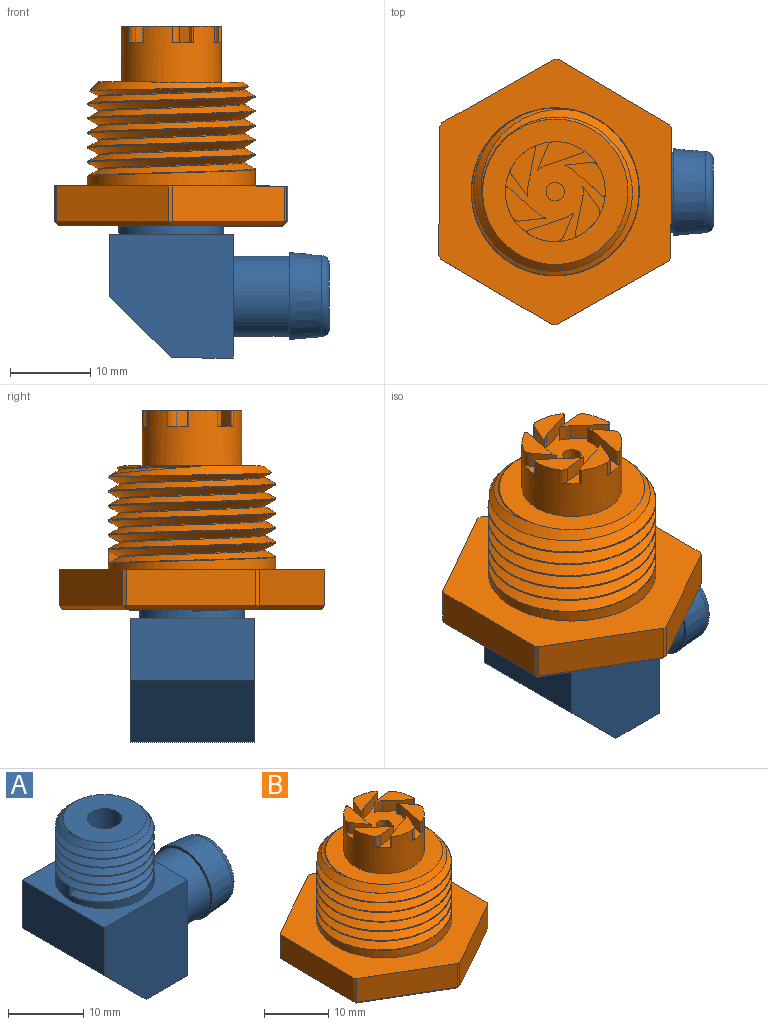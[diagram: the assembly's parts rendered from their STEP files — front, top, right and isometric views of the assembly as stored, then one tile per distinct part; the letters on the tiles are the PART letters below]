
ASSEMBLY  parts=2 mates=1
PART A: 29 faces, bbox 27.5x15.5x26.2 mm
  f0: plane 15.5x15.5mm, normal (0,1,0), area 210.2mm2, adj f1,f10,f11,f12,f28
  f1: plane 15.5x7.75mm, normal (-1,0,0), area 120.1mm2, adj f0,f2,f11,f28
  f2: plane 15.5x15.5mm, normal (0,-1,0), area 210.2mm2, adj f1,f10,f11,f12,f28
  f3: cylinder r=6.56mm len=13.13mm, axis (0,0,-1), area 63.7mm2, adj f4,f11,f22,f27
  f4: cylinder r=6.56mm len=13.13mm, axis (0,0,-1), area 0.1mm2, adj f3,f5,f23,f27
  f5: cylinder r=6.56mm len=13.13mm, axis (0,0,-1), area 0.1mm2, adj f4,f6,f23,f27
  f6: cylinder r=6.56mm len=13.13mm, axis (0,0,-1), area 0.1mm2, adj f5,f7,f23,f27
  f7: cylinder r=6.56mm len=13.13mm, axis (0,0,-1), area 0.1mm2, adj f6,f8,f23,f27
  f8: cylinder r=6.56mm len=13.13mm, axis (0,0,-1), area 0mm2, adj f7,f21,f23,f27
  f9: cylinder r=5mm len=10mm, axis (-1,0,0), area 219.9mm2, adj f10,f16
  f10: plane 15.5x15.5mm, normal (1,0,0), area 161.7mm2, adj f0,f2,f9,f11,f12
  f11: plane 15.5x15.5mm, normal (0,0,1), area 104.8mm2, adj f0,f1,f2,f3,f10
  f12: plane 15.5x7.75mm, normal (0,0,-1), area 120.1mm2, adj f0,f2,f10,f28
  f13: cylinder r=2.3mm len=10.75mm, axis (0,0,-1), area 155.4mm2, adj f14,f19
  f14: plane 11.04x11.03mm, normal (0,0,1), area 78.9mm2, adj f13,f21,f25
  f15: cone r=5mm half-angle=5deg, axis (-1,0,0), area 135.6mm2, adj f16,f20
  f16: plane 10.88x10.88mm, normal (-1,0,0), area 14.3mm2, adj f9,f15
  f17: cylinder r=2.3mm len=12.75mm, axis (-1,0,0), area 184.3mm2, adj f18,f19
  f18: plane 8.17x8.17mm, normal (1,0,0), area 35.8mm2, adj f17,f20
  f19: torus R=7mm, axis (0,-1,0), area 158.9mm2, adj f13,f17
  f20: torus R=4.08mm, axis (1,0,0), area 43.8mm2, adj f15,f18
  f21: cone r=5.51mm half-angle=45deg, axis (0,0,-1), area 27.1mm2, adj f8,f14,f23,f24,f25,f26,f27
  f22: plane 1.41x1.07mm, normal (0,-1,0), area 0.7mm2, adj f3,f23,f24,f25,f26,f27
  f23: bspline ~15.16x13.13mm, area 16.5mm2, adj f4,f5,f6,f7,f8,f21,f22,f24
  f24: bspline ~15.07x13.05mm, area 230.4mm2, adj f21,f22,f23,f25
  f25: bspline ~12.81x11.09mm, area 34.8mm2, adj f14,f21,f22,f24,f26
  f26: bspline ~15.07x13.05mm, area 252.3mm2, adj f21,f22,f25,f27
  f27: bspline ~15.16x13.13mm, area 19.8mm2, adj f3,f4,f5,f6,f7,f8,f21,f22
  f28: plane 15.5x7.75mm, normal (-0.71,0,-0.71), area 169.9mm2, adj f0,f1,f2,f12
PART B: 91 faces, bbox 29.2x33.2x25.6 mm
  f0: cylinder r=5.85mm len=11.69mm, axis (0,0,1), area 25.2mm2, adj f55,f65,f67
  f1: cylinder r=10.5mm len=21mm, axis (0,0,-1), area 107.4mm2, adj f2,f52,f58,f63
  f2: cylinder r=10.5mm len=21mm, axis (0,0,-1), area 0.5mm2, adj f1,f3,f59,f63
  f3: cylinder r=10.5mm len=21mm, axis (0,0,-1), area 0.5mm2, adj f2,f4,f59,f63
  f4: cylinder r=10.5mm len=21mm, axis (0,0,-1), area 0.5mm2, adj f3,f5,f59,f63
  f5: cylinder r=10.5mm len=21mm, axis (0,0,-1), area 0.5mm2, adj f4,f6,f59,f63
  f6: cylinder r=10.5mm len=21mm, axis (0,0,-1), area 0.5mm2, adj f5,f57,f59,f63
  f7: plane 5.08x4.27mm, normal (0,0,1), area 9.6mm2, adj f30,f31,f32,f35,f36,f44
  f8: plane 5.83x3.59mm, normal (0,0,1), area 9.6mm2, adj f26,f27,f28,f29,f32,f43
  f9: plane 6.26x3.1mm, normal (0,0,1), area 9.6mm2, adj f22,f23,f24,f25,f32,f42
  f10: plane 5.08x4.27mm, normal (0,0,1), area 9.6mm2, adj f18,f19,f20,f21,f32,f41
  f11: plane 5.83x3.59mm, normal (0,0,1), area 9.6mm2, adj f14,f15,f16,f17,f32,f40
  f12: cylinder r=0.2mm len=2mm, axis (0,0,1), area 0.9mm2, adj f13,f32,f33,f39
  f13: plane 4.7x2mm, normal (0.98,-0.2,0), area 9.6mm2, adj f12,f33,f39,f45
  f14: plane 3x2mm, normal (-0.92,0.4,0), area 6.5mm2, adj f11,f15,f39,f40
  f15: cylinder r=0.97mm len=2mm, axis (0,0,1), area 2.2mm2, adj f11,f14,f32,f39
  f16: cylinder r=0.2mm len=2mm, axis (0,0,1), area 0.9mm2, adj f11,f17,f32,f39
  f17: plane 4.55x2mm, normal (0.32,-0.95,0), area 9.6mm2, adj f11,f16,f39,f40
  f18: plane 3.25x2mm, normal (-0.11,0.99,0), area 6.5mm2, adj f10,f19,f39,f41
  f19: cylinder r=0.97mm len=2mm, axis (0,0,1), area 2.2mm2, adj f10,f18,f32,f39
  f20: cylinder r=0.2mm len=2mm, axis (0,0,1), area 0.9mm2, adj f10,f21,f32,f39
  f21: plane 3.6x3.17mm, normal (-0.66,-0.75,0), area 9.6mm2, adj f10,f20,f39,f41
  f22: plane 2.63x2mm, normal (0.8,0.6,0), area 6.5mm2, adj f9,f23,f39,f42
  f23: cylinder r=0.97mm len=2mm, axis (0,0,1), area 2.2mm2, adj f9,f22,f32,f39
  f24: cylinder r=0.2mm len=2mm, axis (0,0,1), area 0.9mm2, adj f9,f25,f32,f39
  f25: plane 4.7x2mm, normal (-0.98,0.2,0), area 9.6mm2, adj f9,f24,f39,f42
  f26: plane 3x2mm, normal (0.92,-0.4,0), area 6.5mm2, adj f8,f27,f39,f43
  f27: cylinder r=0.97mm len=2mm, axis (0,0,1), area 2.2mm2, adj f8,f26,f32,f39
  f28: cylinder r=0.2mm len=2mm, axis (0,0,1), area 0.9mm2, adj f8,f29,f32,f39
  f29: plane 4.55x2mm, normal (-0.32,0.95,0), area 9.6mm2, adj f8,f28,f39,f43
  f30: plane 3.25x2mm, normal (0.11,-0.99,0), area 6.5mm2, adj f7,f31,f39,f44
  f31: cylinder r=0.97mm len=2mm, axis (0,0,1), area 2.2mm2, adj f7,f30,f32,f39
  f32: cylinder r=6.25mm len=12.5mm, axis (0,0,1), area 241.6mm2, adj f7,f8,f9,f10,f11,f12,f15,f16
  f33: plane 6.26x3.1mm, normal (0,0,1), area 9.6mm2, adj f12,f13,f32,f37,f38,f45
  f34: plane 18.18x18.18mm, normal (0,0,1), area 136.7mm2, adj f32,f57
  f35: cylinder r=0.2mm len=2mm, axis (0,0,1), area 0.9mm2, adj f7,f32,f36,f39
  f36: plane 3.6x3.17mm, normal (0.66,0.75,0), area 9.6mm2, adj f7,f35,f39,f44
  f37: plane 2.63x2mm, normal (-0.8,-0.6,0), area 6.5mm2, adj f33,f38,f39,f45
  f38: cylinder r=0.97mm len=2mm, axis (0,0,1), area 2.2mm2, adj f32,f33,f37,f39
  f39: plane 12.5x12.47mm, normal (0,0,1), area 61mm2, adj f12,f13,f14,f15,f16,f17,f18,f19
  f40: extruded ~2x1.15mm, area 2.7mm2, adj f11,f14,f17,f39
  f41: extruded ~2x1.14mm, area 2.7mm2, adj f10,f18,f21,f39
  f42: extruded ~2x1.32mm, area 2.7mm2, adj f9,f22,f25,f39
  f43: extruded ~2x1.15mm, area 2.7mm2, adj f8,f26,f29,f39
  f44: extruded ~2x1.14mm, area 2.7mm2, adj f7,f30,f36,f39
  f45: extruded ~2x1.32mm, area 2.7mm2, adj f13,f33,f37,f39
  f46: plane 13.93x8.21mm, normal (0.51,0.86,0), area 72.7mm2, adj f52,f80,f86,f89
  f47: plane 14.07x7.96mm, normal (-0.49,0.87,0), area 72.7mm2, adj f52,f74,f80,f81
  f48: plane 16.17x4.5mm, normal (-1,0.01,0), area 72.7mm2, adj f52,f72,f74,f75
  f49: plane 13.93x8.21mm, normal (-0.51,-0.86,0), area 72.7mm2, adj f52,f72,f76,f77
  f50: plane 14.07x7.96mm, normal (0.49,-0.87,0), area 72.7mm2, adj f52,f77,f82,f83
  f51: plane 16.17x4.5mm, normal (1,-0.01,0), area 72.7mm2, adj f52,f83,f87,f89
  f52: plane 33.2x29.14mm, normal (0,0,1), area 381.9mm2, adj f1,f46,f47,f48,f49,f50,f51,f72
  f53: plane 32.35x28.16mm, normal (0,0,-1), area 529.6mm2, adj f64,f69,f75,f76,f81,f82,f86,f87
  f54: cone r=2.13mm half-angle=4deg, axis (0,0,-1), area 140.6mm2, adj f39,f90
  f55: plane 11.69x11.69mm, normal (0,0,-1), area 107.3mm2, adj f0,f66
  f56: cylinder r=5.85mm len=11.69mm, axis (0,0,1), area 0mm2, adj f64,f67,f71
  f57: cone r=9.09mm half-angle=45deg, axis (0,0,-1), area 60.1mm2, adj f6,f34,f59,f60,f61,f62,f63
  f58: plane 1.82x1.42mm, normal (-1,0,0), area 1.3mm2, adj f1,f59,f60,f61,f62,f63
  f59: bspline ~24.24x21mm, area 27.6mm2, adj f2,f3,f4,f5,f6,f57,f58,f60
  f60: bspline ~24.15x20.92mm, area 528.9mm2, adj f57,f58,f59,f61
  f61: bspline ~21.08x18.26mm, area 59.9mm2, adj f57,f58,f60,f62
  f62: bspline ~24.15x20.92mm, area 577.7mm2, adj f57,f58,f61,f63
  f63: bspline ~24.24x21mm, area 32.9mm2, adj f1,f2,f3,f4,f5,f6,f57,f58
  f64: cone r=6.9mm half-angle=45deg, axis (0,0,-1), area 30.1mm2, adj f53,f56,f67,f68,f69,f70,f71
  f65: plane 1.42x1.07mm, normal (0,-1,0), area 0.7mm2, adj f0,f66,f67,f68,f69,f70,f71
  f66: cylinder r=5.85mm len=0.51mm, axis (0,0,1), area 0mm2, adj f55,f65,f67
  f67: bspline ~13.56x12.2mm, area 17.4mm2, adj f0,f56,f64,f65,f66,f68
  f68: bspline ~15.82x14.23mm, area 262.1mm2, adj f64,f65,f67,f69
  f69: bspline ~15.96x14.35mm, area 42.8mm2, adj f53,f64,f65,f68,f70
  f70: bspline ~15.82x14.23mm, area 240mm2, adj f64,f65,f69,f71
  f71: bspline ~13.56x12.2mm, area 14.5mm2, adj f56,f64,f65,f70
  f72: plane 4.5x0.44mm, normal (-0.87,-0.49,0), area 2.2mm2, adj f48,f49,f52,f73
  f73: plane 0.5x0.5mm, normal (-0.66,-0.37,-0.65), area 0.2mm2, adj f72,f75,f76
  f74: plane 4.5x0.43mm, normal (-0.86,0.51,0), area 2.2mm2, adj f47,f48,f52,f78
  f75: plane 16.17x0.65mm, normal (-0.71,0.01,-0.71), area 11.4mm2, adj f48,f53,f73,f78
  f76: plane 14.18x8.64mm, normal (-0.36,-0.61,-0.71), area 11.4mm2, adj f49,f53,f73,f79
  f77: plane 4.5x0.5mm, normal (-0.01,-1,0), area 2.2mm2, adj f49,f50,f52,f79
  f78: plane 0.5x0.5mm, normal (-0.65,0.38,-0.65), area 0.2mm2, adj f74,f75,f81
  f79: plane 0.5x0.5mm, normal (-0.01,-0.76,-0.65), area 0.2mm2, adj f76,f77,f82
  f80: plane 4.5x0.5mm, normal (0.01,1,0), area 2.2mm2, adj f46,f47,f52,f84
  f81: plane 14.32x8.39mm, normal (-0.35,0.62,-0.71), area 11.4mm2, adj f47,f53,f78,f84
  f82: plane 14.32x8.39mm, normal (0.35,-0.62,-0.71), area 11.4mm2, adj f50,f53,f79,f85
  f83: plane 4.5x0.43mm, normal (0.86,-0.51,0), area 2.2mm2, adj f50,f51,f52,f85
  f84: plane 0.5x0.5mm, normal (0.01,0.76,-0.65), area 0.2mm2, adj f80,f81,f86
  f85: plane 0.5x0.5mm, normal (0.65,-0.38,-0.65), area 0.2mm2, adj f82,f83,f87
  f86: plane 14.18x8.64mm, normal (0.36,0.61,-0.71), area 11.4mm2, adj f46,f53,f84,f88
  f87: plane 16.17x0.65mm, normal (0.71,-0.01,-0.71), area 11.4mm2, adj f51,f53,f85,f88
  f88: plane 0.5x0.5mm, normal (0.66,0.37,-0.65), area 0.2mm2, adj f86,f87,f89
  f89: plane 4.5x0.44mm, normal (0.87,0.49,0), area 2.2mm2, adj f46,f51,f52,f88
  f90: plane 4.22x4.22mm, normal (0,0,1), area 14mm2, adj f54
PLACE A rot(axis=(0,1,0),0deg) t=(-24.36,-4.86,-20.1)mm
PLACE B rot(axis=(0,1,0),0deg) t=(-24.36,-4.86,-3.6)mm
MATE fastened A.f13 <-> B.f0  axis (0,0,1) through (-24.36,-4.86,5.4)mm
